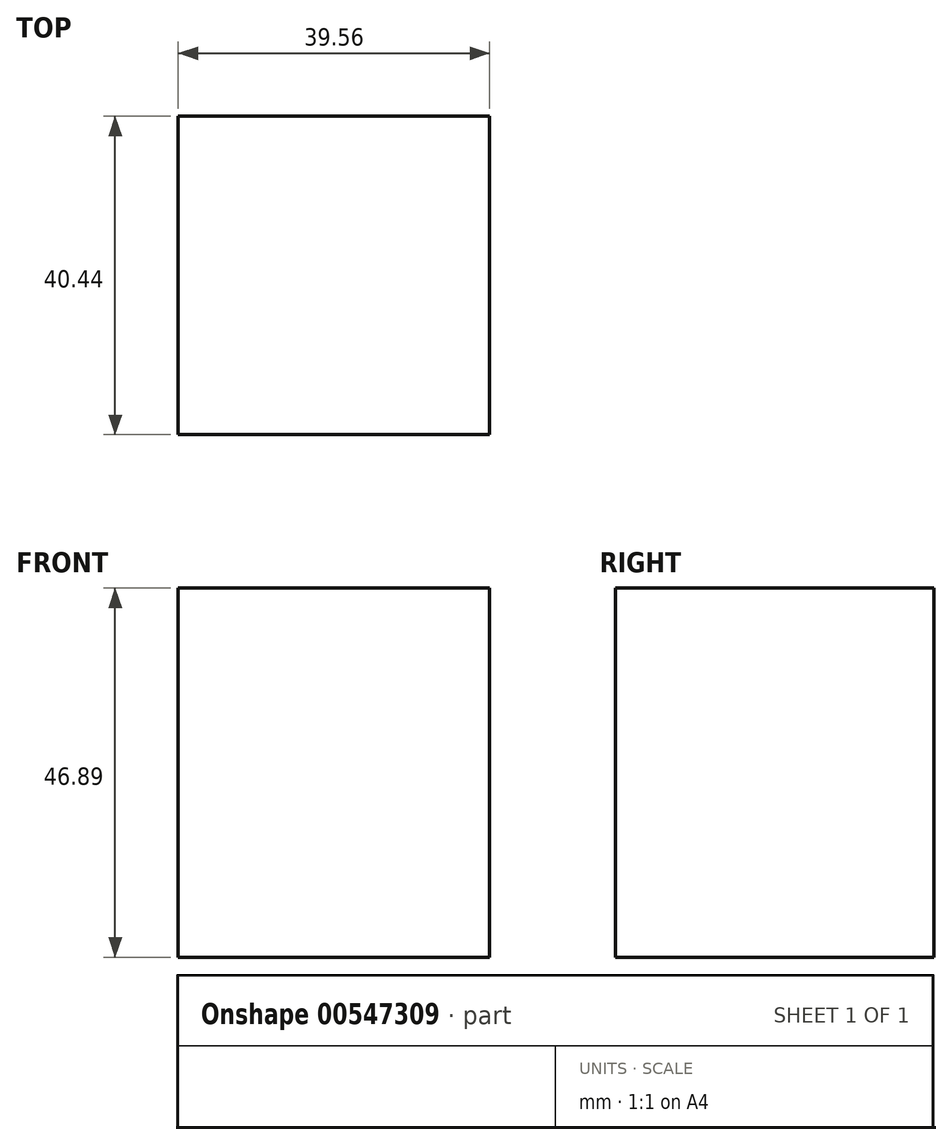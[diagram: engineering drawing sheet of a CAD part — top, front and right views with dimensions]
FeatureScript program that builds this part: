
annotation { "Feature Type Name" : "Feature", "Feature Type Description" : "" }
export const myFeature = defineFeature(function(context is Context, id is Id, definition is map)
    precondition{}
    {
        {
            var Q0;
            Q0=qCreatedBy(makeId("Top.planeOp"),FACE);
            var sketch = newSketch(context, id + "F0", { "sketchPlane" : qUnion([Q0])});
            skLineSegment(sketch, "E0.bottom", {"start": v(0, 0) * mm, "end": v(39.56, 0) * mm});
            skLineSegment(sketch, "E0.top", {"start": v(0, 40.44) * mm, "end": v(39.56, 40.44) * mm});
            skLineSegment(sketch, "E0.left", {"start": v(0, 0) * mm, "end": v(0, 40.44) * mm});
            skLineSegment(sketch, "E0.right", {"start": v(39.56, 0) * mm, "end": v(39.56, 40.44) * mm});
            skSolve(sketch);
        }
        {
            var Q0;
            Q0 = qSketchRegion(id + "F0", true);
            extrude(context, id + "F1", {"entities" : qUnion([Q0]), "depth" : 46.9 * mm, "offsetDistance" : 25.4 * mm});
        }
    });
